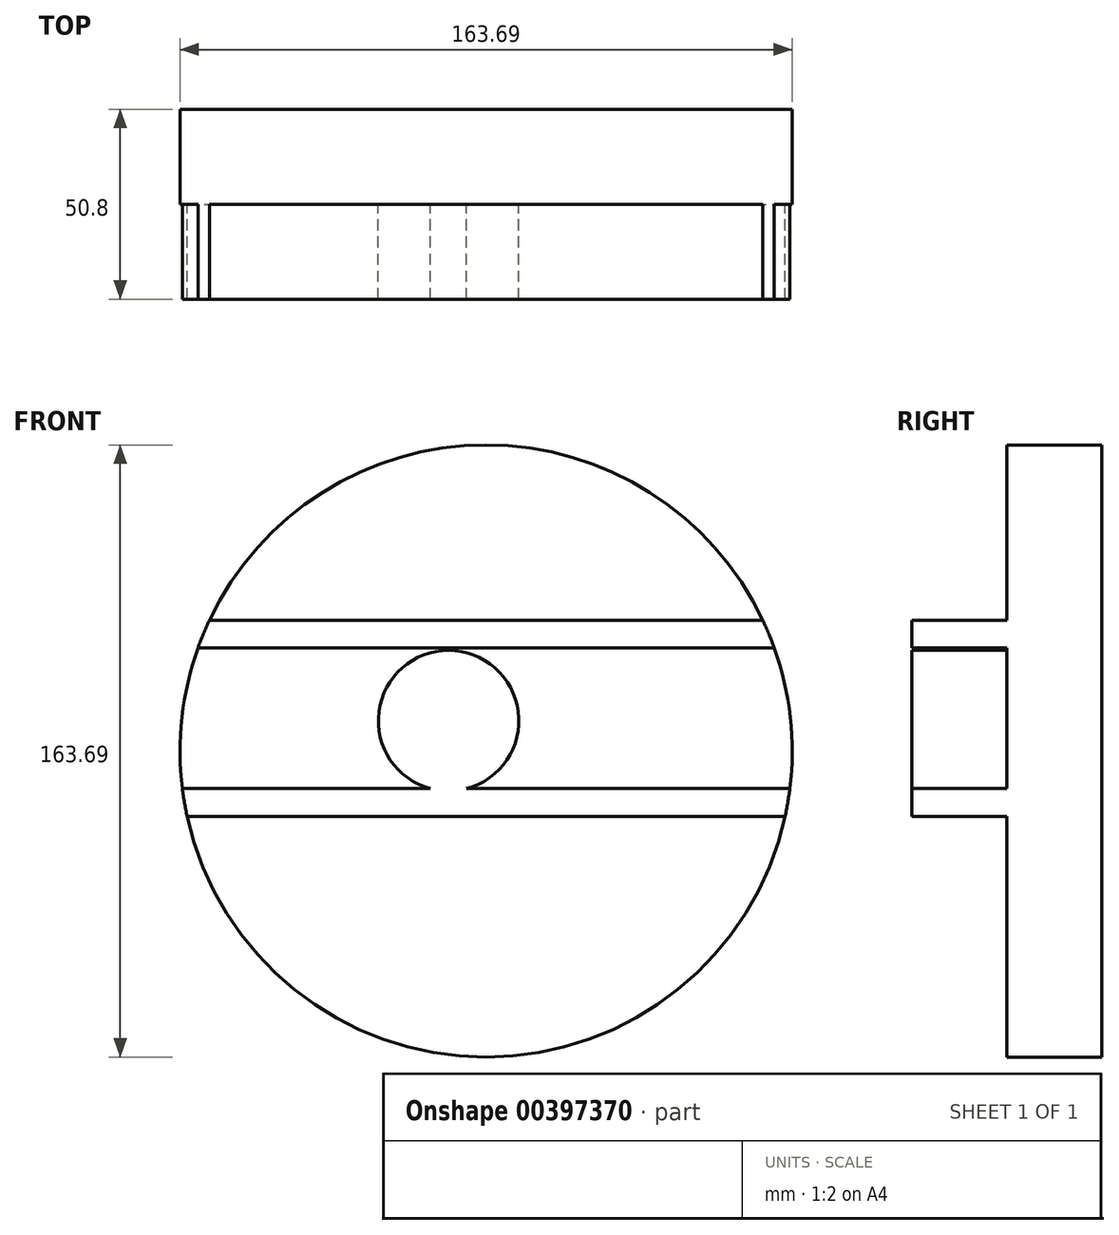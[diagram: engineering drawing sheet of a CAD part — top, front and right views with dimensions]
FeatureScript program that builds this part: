
annotation { "Feature Type Name" : "Feature", "Feature Type Description" : "" }
export const myFeature = defineFeature(function(context is Context, id is Id, definition is map)
    precondition{}
    {
        {
            var Q0;
            Q0=qCreatedBy(makeId("Front.planeOp"),FACE);
            var sketch = newSketch(context, id + "F0", { "sketchPlane" : qUnion([Q0])});
            skCircle(sketch, "E0", {"center": v(-4.8, 4.45) * mm, "radius": 81.85 * mm});
            skSolve(sketch);
        }
        {
            var Q0;
            Q0 = qSketchRegion(id + "F0", true);
            extrude(context, id + "F1", {"entities" : qUnion([Q0]), "depth" : 25.4 * mm});
        }
        {
            var Q0;
            Q0=makeQuery(id+"F1.opExtrude","CAP_FACE",FACE,{"disambiguationData":[OSD([sQuery(id+"F0.wireOp",EDGE,"E0")])],"isStart":false});
            var sketch = newSketch(context, id + "F2", { "sketchPlane" : qUnion([Q0])});
            skLineSegment(sketch, "E1", {"start": v(-81.85, 32.06) * mm, "end": v(72.24, 32.06) * mm});
            skLineSegment(sketch, "E2", {"start": v(-78.8, 39.41) * mm, "end": v(69.2, 39.41) * mm});
            skCircle(sketch, "E3", {"center": v(-14.85, 12.54) * mm, "radius": 18.79 * mm});
            skLineSegment(sketch, "E4", {"start": v(-86.03, -5.62) * mm, "end": v(76.42, -5.62) * mm});
            skLineSegment(sketch, "E5", {"start": v(-84.75, -13.07) * mm, "end": v(75.14, -13.07) * mm});
            skSolve(sketch);
        }
        {
            var Q0;
            Q0 = qSketchRegion(id + "F2", true);
            var Q1;
            {var subQ0=sQuery(id+"F2.wireOp",EDGE,"E1");Q1=makeQuery(id+"F2.imprint","IMPRINT",FACE,{"disambiguationData":[TD([[makeQuery(id+"F2.imprint","IMPRINT",EDGE,{"derivedFrom":subQ0}),1.0]])]});}
            var Q2;
            {var subQ7=sQuery(id+"F2.wireOp",EDGE,"E5");Q2=makeQuery(id+"F2.imprint","IMPRINT",FACE,{"disambiguationData":[TD([[makeQuery(id+"F2.imprint","IMPRINT",EDGE,{"derivedFrom":subQ7}),1.0]])]});}
            extrude(context, id + "F3", {"entities" : qUnion([Q0, Q1, Q2]), "operationType" : NewBodyOperationType.ADD, "depth" : 25.4 * mm});
        }
    });
